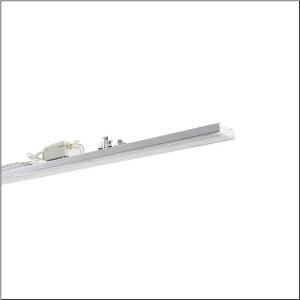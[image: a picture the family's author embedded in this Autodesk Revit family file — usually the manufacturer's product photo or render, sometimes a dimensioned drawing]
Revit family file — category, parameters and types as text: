
# Revit family: licross_r__21_recessed_mo_52te18dv4e5g_691e
name_source: partatom
category: Lighting Fixtures
units: mm (PartAtom-declared; Revit-internal decimal feet)

## family parameters
Cut with Voids When Loaded = No
Host = Face
Light Source = No
Part Type = Normal
Room Calculation Point = No
Round Connector Dimension = Use Diameter
Shared = No

## types (1)
- --- (1 x LED, 14980 lm, 85.3 W, 4000K)
    Apparent Load = 85 VA
    CIE Flux Codes = 79 95 99 100 100
    Color Rendering = 80
    Color Temperature = 4000K
    Default Elevation = 1800 mm
    Description = Licross® 21 Recessed MO, luminaire insert, of sheet steel, galvanised, coil coated, white, length: 2.250mm, width: 66mm, height: 67mm, LED rated luminous flux: 14.980lm, light colour: 840, control gear: DALI 2, with plug, 5-pole, with phase selection, mains connection: 220..240V, AC, 50/60Hz, rated input power: 85W, halogen-free wiring, primary light control with lens, of plastic, primary optical cover: cover, of PMMA, light emission: direct distribution, primary light characteristic: symmetric, protection rating (complete): IP54, insulation class (complete): insulation class I (protective earthing), certification: CE, ENEC, VDE, UKCA, protection symbol: D if used in an environment with non-conductive dust loads with corresponding accessories, impact resistance: IK06, permissible ambient temperature for indoor applications: -25..+35°C, corresponds to IFS (International Featured Standards) requirements for safety and quality in the food industry, reducing of maximum allowable ambient temperature of 5°C with ceiling mounting, LABS conformity tested according to VDMA 24364:2018-05, packaging unit: 1 piece
    Height = 58 mm
    Lamp = 1 x LED
    Lamp Light Flux = 14980 lm
    Lamp Power = 85.3 W
    Lamp count = 1
    Length = 2250 mm
    Luminous efficacy = 176 lm/W
    Manufacturer = Siteco
    ModVariant = No
    Model = 52TE18DV4E5G
    Mounting Place = Ceiling
    Mounting Type = Pendant
    Number of Poles = 1
    OnlyDefault = Yes
    Power Factor = 1
    Product Name = Licross® 21 Recessed MO
    Product group = luminaire insert
    ProductGroupID = 901
    Protection Class = Protection class I
    Protection Degree = IP 54
    RLX_Detail_Level = 1
    RLX_Emergency_Light_Flux = 0 lm
    RLX_Emergency_Type = 0
    RLX_Emergency_Type_DB = No
    RlxData = <blob elided: 29517 chars, md5=64042acf>
    Socket = socket
    Standby Power = 0 W
    System Light Flux = 14980 lm
    System Power = 85 W
    Type Comments = factory setting: luminous flux: 100 % | dim-lin: 254 | 390 mA
    Type Image = l_1296930.jpg
    URL = http://relux.com
    VarID = @adj_057543
    Voltage = 0 V
    Weight = 0.00 kg
    Width = 66 mm

## geometry (parser evidence)
native form markers: Blend x4, Sweep x8
no freeform markers — native parametric forms only
